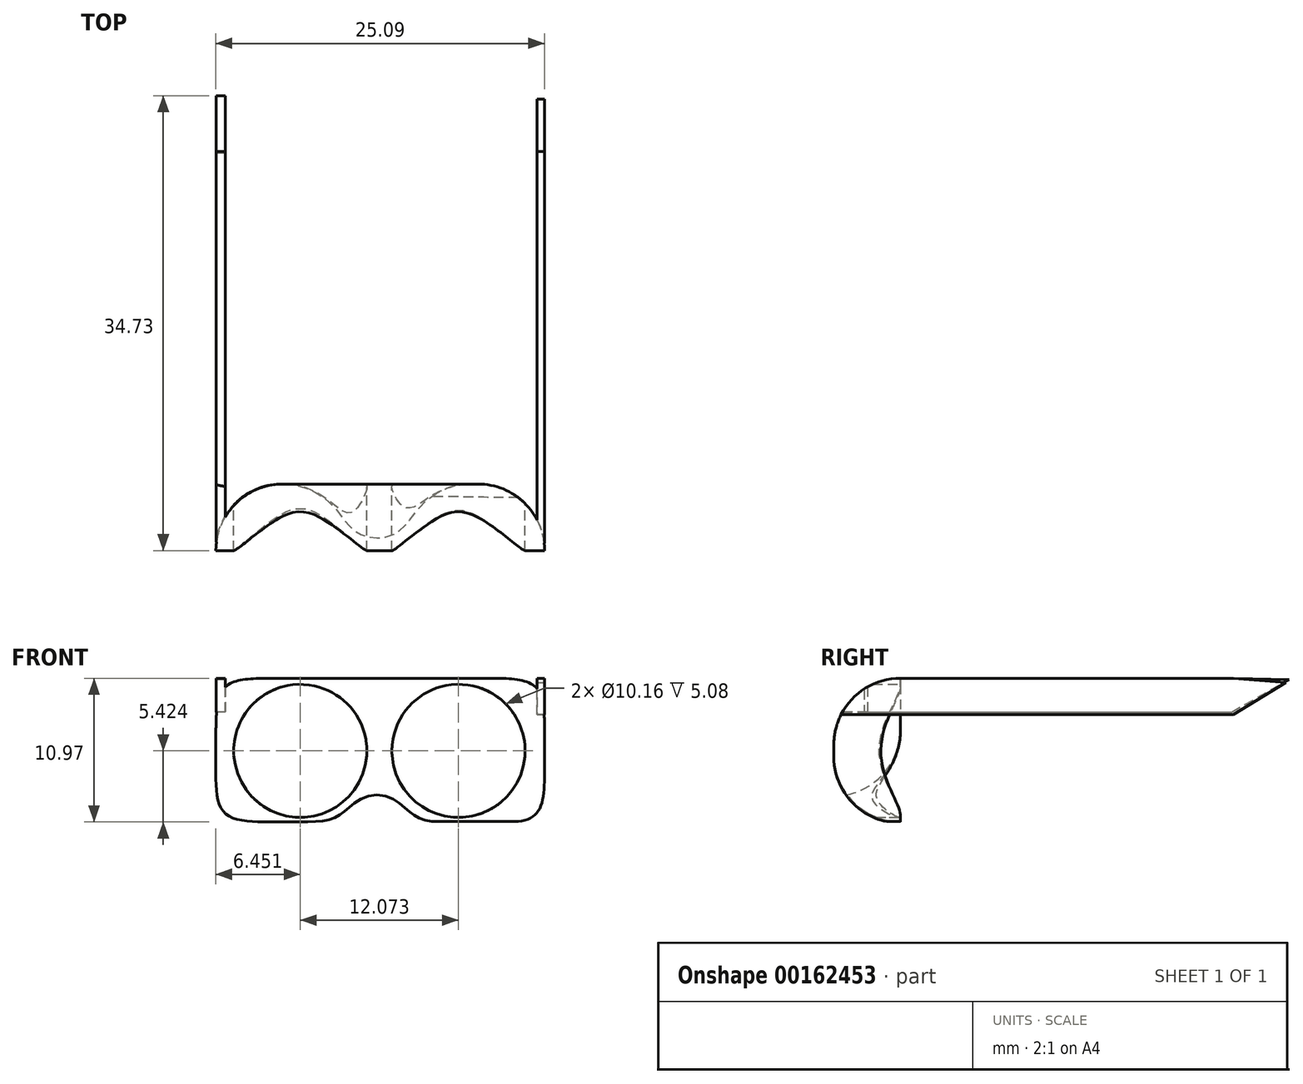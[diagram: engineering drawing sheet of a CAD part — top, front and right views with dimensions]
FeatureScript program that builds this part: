
annotation { "Feature Type Name" : "Feature", "Feature Type Description" : "" }
export const myFeature = defineFeature(function(context is Context, id is Id, definition is map)
    precondition{}
    {
        {
            var Q0;
            Q0=qCreatedBy(makeId("Front.planeOp"),FACE);
            var sketch = newSketch(context, id + "F0", { "sketchPlane" : qUnion([Q0])});
            skLineSegment(sketch, "E0", {"start": v(12.65, 16.05) * mm, "end": v(12.65, 5.1) * mm});
            skLineSegment(sketch, "E1", {"start": v(12.65, 5.1) * mm, "end": v(1.92, 5.12) * mm});
            skLineSegment(sketch, "E2", {"start": v(-2.2, 5.06) * mm, "end": v(-12.46, 5.1) * mm});
            skCircle(sketch, "E3", {"center": v(-5.99, 10.5) * mm, "radius": 5.08 * mm});
            skCircle(sketch, "E4", {"center": v(6.08, 10.5) * mm, "radius": 5.08 * mm});
            skLineSegment(sketch, "E5", {"start": v(-12.46, 5.1) * mm, "end": v(-12.4, 16.05) * mm});
            skLineSegment(sketch, "E6", {"start": v(-12.4, 16.05) * mm, "end": v(12.65, 16.05) * mm});
            skArc(sketch, "E7", {"start": v(1.92, 5.12) * mm, "mid": v(-0.17, 7.05) * mm, "end": v(-2.2, 5.06) * mm});
            skLineSegment(sketch, "E8", {"start": v(-1.03, 11.6) * mm, "end": v(1.12, 11.6) * mm});
            skLineSegment(sketch, "E9", {"start": v(1.12, 11.6) * mm, "end": v(1.01, 10.2) * mm});
            skLineSegment(sketch, "E10", {"start": v(1.01, 10.2) * mm, "end": v(-0.92, 10.2) * mm});
            skLineSegment(sketch, "E11", {"start": v(-0.92, 10.2) * mm, "end": v(-1.03, 11.6) * mm});
            skSolve(sketch);
        }
        {
            var Q0;
            Q0=makeQuery(id+"F0.imprint","IMPRINT",FACE,{"disambiguationData":[TD([[makeQuery(id+"F0.imprint","IMPRINT",EDGE,{"derivedFrom":sQuery(id+"F0.wireOp",EDGE,"E0")}),-1.0]])]});
            var Q1;
            {var subQ1=sQuery(id+"F0.wireOp",EDGE,"E8");Q1=makeQuery(id+"F0.imprint","IMPRINT",FACE,{"disambiguationData":[TD([[makeQuery(id+"F0.imprint","IMPRINT",EDGE,{"derivedFrom":subQ1}),-1.0]])]});}
            extrude(context, id + "F1", {"entities" : qUnion([Q0, Q1]), "depth" : 5.08 * mm});
        }
        {
            var Q0;
            Q0=makeQuery(id+"F1.opExtrude","SWEPT_FACE",FACE,{"disambiguationData":[OSD([sQuery(id+"F0.wireOp",EDGE,"E0")])]});
            var sketch = newSketch(context, id + "F2", { "sketchPlane" : qUnion([Q0])});
            skLineSegment(sketch, "E12", {"start": v(0, 16.05) * mm, "end": v(25.4, 16.05) * mm});
            skLineSegment(sketch, "E13", {"start": v(25.4, 16.05) * mm, "end": v(25.4, 13.27) * mm});
            skLineSegment(sketch, "E14", {"start": v(25.4, 13.27) * mm, "end": v(0, 13.27) * mm});
            skLineSegment(sketch, "E15", {"start": v(0, 13.27) * mm, "end": v(0, 16.05) * mm});
            skLineSegment(sketch, "E16", {"start": v(25.4, 16.05) * mm, "end": v(29.4, 15.74) * mm});
            skLineSegment(sketch, "E17", {"start": v(29.4, 15.74) * mm, "end": v(25.4, 13.27) * mm});
            skSolve(sketch);
        }
        {
            var Q0;
            Q0=makeQuery(id+"F2.imprint","IMPRINT",FACE,{"disambiguationData":[TD([[makeQuery(id+"F2.imprint","IMPRINT",EDGE,{"derivedFrom":sQuery(id+"F2.wireOp",EDGE,"E12")}),-1.0]])]});
            var Q1;
            Q1=makeQuery(id+"F2.imprint","IMPRINT",FACE,{"disambiguationData":[TD([[makeQuery(id+"F2.imprint","IMPRINT",EDGE,{"derivedFrom":sQuery(id+"F2.wireOp",EDGE,"E13")}),1.0]])]});
            extrude(context, id + "F3", {"entities" : qUnion([Q0, Q1]), "operationType" : NewBodyOperationType.ADD, "oppositeDirection" : true, "depth" : 0.57 * mm});
        }
        {
            var Q0;
            Q0=makeQuery(id+"F1.opExtrude","SWEPT_FACE",FACE,{"disambiguationData":[OSD([sQuery(id+"F0.wireOp",EDGE,"E5")])]});
            var sketch = newSketch(context, id + "F4", { "sketchPlane" : qUnion([Q0])});
            skLineSegment(sketch, "E18", {"start": v(0, 15.99) * mm, "end": v(0, 13.4) * mm});
            skLineSegment(sketch, "E19", {"start": v(0, 13.4) * mm, "end": v(-25.27, 13.4) * mm});
            skLineSegment(sketch, "E20", {"start": v(0, 15.99) * mm, "end": v(-25.4, 15.99) * mm});
            skLineSegment(sketch, "E21", {"start": v(-25.27, 13.4) * mm, "end": v(-25.4, 15.99) * mm});
            skLineSegment(sketch, "E22", {"start": v(-25.27, 13.4) * mm, "end": v(-29.65, 15.9) * mm});
            skLineSegment(sketch, "E23", {"start": v(-29.65, 15.9) * mm, "end": v(-25.4, 15.99) * mm});
            skSolve(sketch);
        }
        {
            var Q0;
            Q0=makeQuery(id+"F4.imprint","IMPRINT",FACE,{"disambiguationData":[TD([[makeQuery(id+"F4.imprint","IMPRINT",EDGE,{"derivedFrom":sQuery(id+"F4.wireOp",EDGE,"E21")}),1.0]])]});
            var Q1;
            Q1=makeQuery(id+"F4.imprint","IMPRINT",FACE,{"disambiguationData":[TD([[makeQuery(id+"F4.imprint","IMPRINT",EDGE,{"derivedFrom":sQuery(id+"F4.wireOp",EDGE,"E18")}),1.0]])]});
            extrude(context, id + "F5", {"entities" : qUnion([Q0, Q1]), "operationType" : NewBodyOperationType.ADD, "oppositeDirection" : true, "depth" : 0.7 * mm});
        }
        {
            var Q0;
            Q0=makeQuery(id+"F1.opExtrude","CAP_EDGE",EDGE,{"disambiguationData":[OSD([sQuery(id+"F0.wireOp",EDGE,"E2")])],"isStart":false});
            var Q1;
            Q1=makeQuery(id+"F1.opExtrude","CAP_EDGE",EDGE,{"disambiguationData":[OSD([sQuery(id+"F0.wireOp",EDGE,"E6")])],"isStart":false});
            fillet(context, id + "F6", {"entities" : qUnion([Q0, Q1]), "radius" : 5.08 * mm, "tangentPropagation" : true, "allowEdgeOverflow" : false});
        }
        {
            var Q0;
            Q0=makeQuery(id+"F1.opExtrude","CAP_EDGE",EDGE,{"disambiguationData":[OSD([sQuery(id+"F0.wireOp",EDGE,"E7")])],"isStart":true});
            var Q1;
            Q1=makeQuery(id+"F1.opExtrude","CAP_EDGE",EDGE,{"disambiguationData":[OSD([sQuery(id+"F0.wireOp",EDGE,"E5")])],"isStart":true});
            var Q2;
            Q2=makeQuery(id+"F1.opExtrude","CAP_EDGE",EDGE,{"disambiguationData":[OSD([sQuery(id+"F0.wireOp",EDGE,"E0")])],"isStart":true});
            fillet(context, id + "F7", {"entities" : qUnion([Q0, Q1, Q2]), "radius" : 5.08 * mm, "tangentPropagation" : true, "allowEdgeOverflow" : false});
        }
    });
